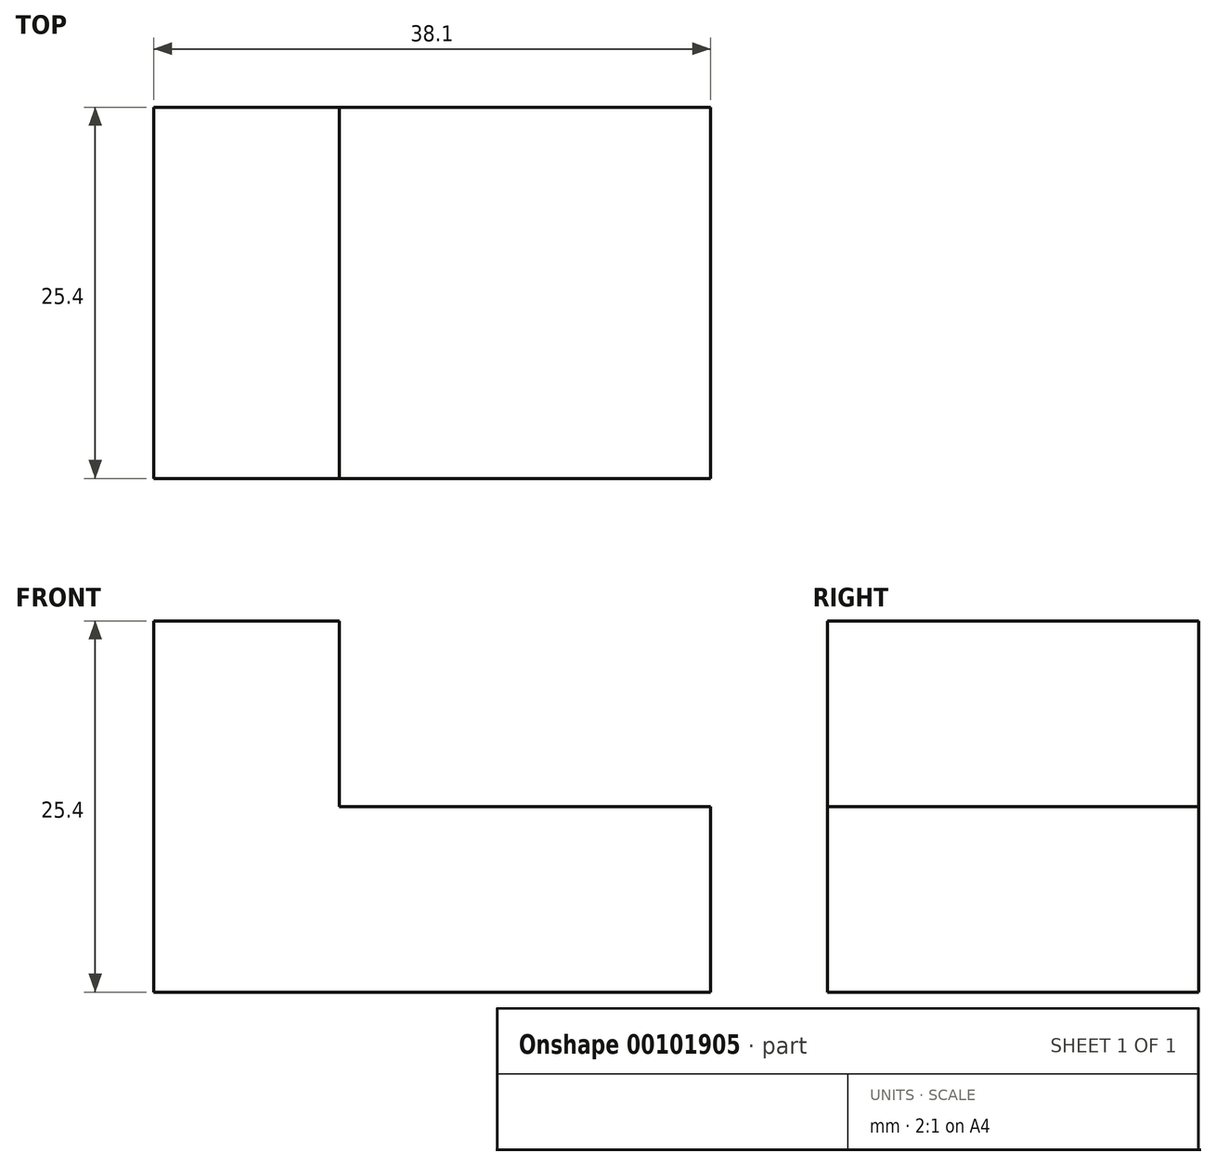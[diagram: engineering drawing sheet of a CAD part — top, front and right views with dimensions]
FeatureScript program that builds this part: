
annotation { "Feature Type Name" : "Feature", "Feature Type Description" : "" }
export const myFeature = defineFeature(function(context is Context, id is Id, definition is map)
    precondition{}
    {
        {
            var Q0;
            Q0=qCreatedBy(makeId("Front.planeOp"),FACE);
            var sketch = newSketch(context, id + "F0", { "sketchPlane" : qUnion([Q0])});
            skLineSegment(sketch, "E0.bottom", {"start": v(0, 0) * mm, "end": v(38.1, 0) * mm});
            skLineSegment(sketch, "E0.top", {"start": v(0, 12.7) * mm, "end": v(38.1, 12.7) * mm});
            skLineSegment(sketch, "E0.left", {"start": v(0, 0) * mm, "end": v(0, 12.7) * mm});
            skLineSegment(sketch, "E0.right", {"start": v(38.1, 0) * mm, "end": v(38.1, 12.7) * mm});
            skSolve(sketch);
        }
        {
            var Q0;
            Q0=makeQuery(id+"F0.imprint","IMPRINT",FACE,{"disambiguationData":[TD([[makeQuery(id+"F0.imprint","IMPRINT",EDGE,{"derivedFrom":sQuery(id+"F0.wireOp",EDGE,"E0.bottom")}),1.0]])]});
            var Q1;
            Q1 = qSketchRegion(id + "F0", true);
            extrude(context, id + "F1", {"entities" : qUnion([Q0, Q1]), "depth" : 25.4 * mm});
        }
        {
            var Q0;
            Q0=makeQuery(id+"F1.opExtrude","SWEPT_FACE",FACE,{"disambiguationData":[OSD([sQuery(id+"F0.wireOp",EDGE,"E0.top")])]});
            var sketch = newSketch(context, id + "F2", { "sketchPlane" : qUnion([Q0])});
            skLineSegment(sketch, "E1.bottom", {"start": v(0, 0) * mm, "end": v(12.7, 0) * mm});
            skLineSegment(sketch, "E1.top", {"start": v(0, -25.4) * mm, "end": v(12.7, -25.4) * mm});
            skLineSegment(sketch, "E1.left", {"start": v(0, 0) * mm, "end": v(0, -25.4) * mm});
            skLineSegment(sketch, "E1.right", {"start": v(12.7, 0) * mm, "end": v(12.7, -25.4) * mm});
            skSolve(sketch);
        }
        {
            var Q0;
            Q0 = qSketchRegion(id + "F2", true);
            extrude(context, id + "F3", {"entities" : qUnion([Q0]), "operationType" : NewBodyOperationType.ADD, "depth" : 12.7 * mm});
        }
    });
